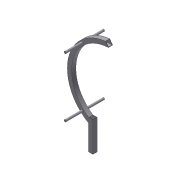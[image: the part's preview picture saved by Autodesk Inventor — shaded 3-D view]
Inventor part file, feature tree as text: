
AUTODESK INVENTOR PART (.ipt)
format: ipt  version: 2012 (Build 160160000, 160)  size: 119,296 bytes
history: native  units: in
note: dims shown in document units (in); Inventor stores cm internally (conversion verified against a paired STEP export)
features: extrude x2, sketch x2, shell x1
ambient origin geometry x8: Origin, YZ Plane, XZ Plane, XY Plane, X Axis, Y Axis, Z Axis, Center Point
feature tree (5):
  extrude  "Extrusion2"  Depth=9.0in
  shell  "Shell2"  Thickness=5.0in
  extrude  "Extrusion3"  Depth=7.0in
  sketch  "Sketch1"  dims[d0=1.0in d1=9.0in d5=5.0in]
  sketch  "Sketch2"  dims[d6=1.0in d7=7.0in d8=1.0in d9=0.0in d10=0.0625in d11=1.5in d12=0.5in d13=4.0in d14=5.0in d15=0.0in d16=0.0in]
